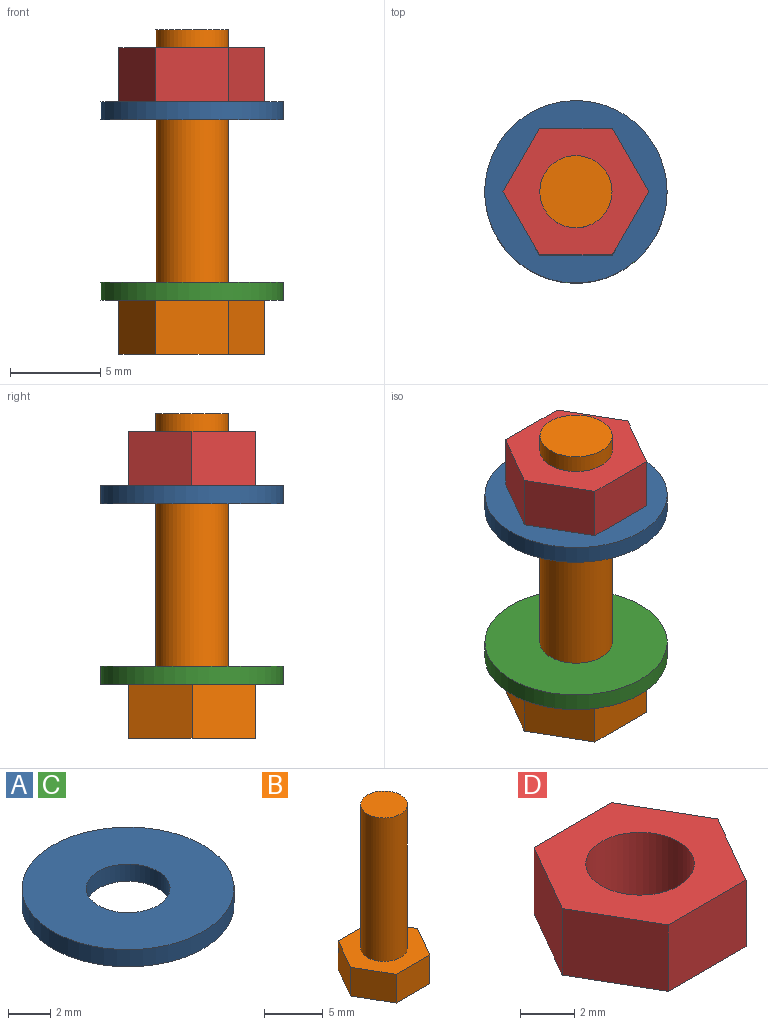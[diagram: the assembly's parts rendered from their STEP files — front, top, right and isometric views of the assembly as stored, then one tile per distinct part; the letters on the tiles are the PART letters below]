
ASSEMBLY  parts=4 mates=3
PART A: 4 faces, bbox 10.1x10.1x1 mm
  f0: cylinder r=2mm len=4mm, axis (0,0,-1), area 12.6mm2, adj f2,f3
  f1: cylinder r=5.05mm len=10.1mm, axis (0,0,-1), area 31.7mm2, adj f2,f3
  f2: plane 10.1x10.1mm, normal (0,0,1), area 67.6mm2, adj f0,f1
  f3: plane 10.1x10.1mm, normal (0,0,-1), area 67.6mm2, adj f0,f1
PART B: 10 faces, bbox 8.1x7x18 mm
  f0: plane 4.04x3mm, normal (0,1,0), area 12.1mm2, adj f1,f5,f6,f7
  f1: plane 3.5x3mm, normal (-0.87,0.5,0), area 12.1mm2, adj f0,f2,f6,f7
  f2: plane 3.5x3mm, normal (-0.87,-0.5,0), area 12.1mm2, adj f1,f3,f6,f7
  f3: plane 4.04x3mm, normal (0,-1,0), area 12.1mm2, adj f2,f4,f6,f7
  f4: plane 3.5x3mm, normal (0.87,-0.5,0), area 12.1mm2, adj f3,f5,f6,f7
  f5: plane 3.5x3mm, normal (0.87,0.5,0), area 12.1mm2, adj f0,f4,f6,f7
  f6: plane 8.08x7mm, normal (0,0,-1), area 42.4mm2, adj f0,f1,f2,f3,f4,f5
  f7: plane 8.08x7mm, normal (0,0,1), area 29.9mm2, adj f0,f1,f2,f3,f4,f5,f8
  f8: cylinder r=2mm len=15mm, axis (0,0,-1), area 188.5mm2, adj f7,f9
  f9: plane 4x4mm, normal (0,0,1), area 12.6mm2, adj f8
PART C: same geometry as A
PART D: 9 faces, bbox 8.1x7x3 mm
  f0: plane 4.04x3mm, normal (0,-1,0), area 12.1mm2, adj f1,f5,f7,f8
  f1: plane 3.5x3mm, normal (0.87,-0.5,0), area 12.1mm2, adj f0,f2,f7,f8
  f2: plane 3.5x3mm, normal (0.87,0.5,0), area 12.1mm2, adj f1,f3,f7,f8
  f3: plane 4.04x3mm, normal (0,1,0), area 12.1mm2, adj f2,f4,f7,f8
  f4: plane 3.5x3mm, normal (-0.87,0.5,0), area 12.1mm2, adj f3,f5,f7,f8
  f5: plane 3.5x3mm, normal (-0.87,-0.5,0), area 12.1mm2, adj f0,f4,f7,f8
  f6: cylinder r=2mm len=4mm, axis (0,0,-1), area 37.7mm2, adj f7,f8
  f7: plane 8.08x7mm, normal (0,0,1), area 29.9mm2, adj f0,f1,f2,f3,f4,f5,f6
  f8: plane 8.08x7mm, normal (0,0,-1), area 29.9mm2, adj f0,f1,f2,f3,f4,f5,f6
PLACE A t=(180,22.92,6)mm
PLACE B t=(180,-19.08,-4)mm
PLACE C t=(180,22.92,-4)mm
PLACE D rot(axis=(1,0,0),180deg) t=(180,-40.08,10)mm
MATE fastened A.f0 <-> C.f0  axis (0,0,-1) through (180,-19.08,6)mm
MATE fastened D.f6 <-> A.f0  axis (0,0,1) through (180,-19.08,7)mm
MATE fastened C.f0 <-> B.f8  axis (0,0,-1) through (180,-19.08,-4)mm
